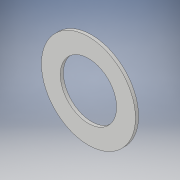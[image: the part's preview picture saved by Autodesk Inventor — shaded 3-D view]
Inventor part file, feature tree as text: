
AUTODESK INVENTOR PART (.ipt)
format: ipt  version: 2019 (Build 230136000, 136)  size: 98,816 bytes
history: native  units: mm
features: extrude x1, sketch x1
ambient origin geometry x8: Origin, YZ Plane, XZ Plane, XY Plane, X Axis, Y Axis, Z Axis, Center Point
bodies: Solid1 (feature_tree)
feature tree (2):
  extrude  "Extrusion1"  Depth=2.0mm TaperAngle=0.0deg
  sketch  "Sketch1"  dims[d0=36.0mm d2=2.0mm d3=0.0mm d4=60.0mm]
